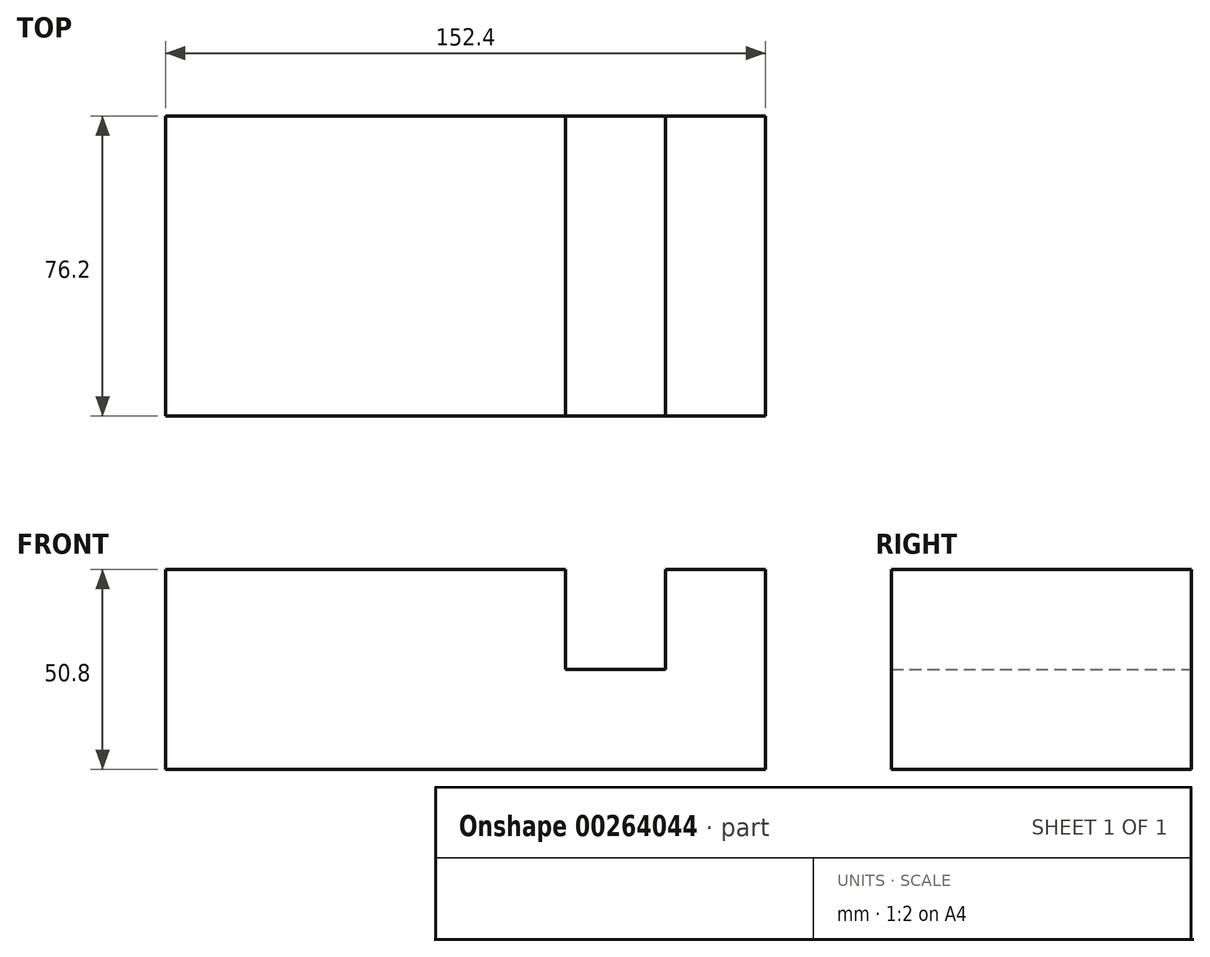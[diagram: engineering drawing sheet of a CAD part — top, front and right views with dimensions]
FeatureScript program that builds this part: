
annotation { "Feature Type Name" : "Feature", "Feature Type Description" : "" }
export const myFeature = defineFeature(function(context is Context, id is Id, definition is map)
    precondition{}
    {
        {
            var Q0;
            Q0=qCreatedBy(makeId("Front.planeOp"),FACE);
            var sketch = newSketch(context, id + "F0", { "sketchPlane" : qUnion([Q0])});
            skLineSegment(sketch, "E0.bottom", {"start": v(25.04, 0) * mm, "end": v(-76.56, 0) * mm});
            skLineSegment(sketch, "E0.right", {"start": v(-76.56, 0) * mm, "end": v(-76.56, 25.4) * mm});
            skLineSegment(sketch, "E1.bottom", {"start": v(75.84, 0) * mm, "end": v(50.44, 0) * mm});
            skLineSegment(sketch, "E1.left", {"start": v(75.84, 0) * mm, "end": v(75.84, 25.4) * mm});
            skLineSegment(sketch, "E2", {"start": v(25.04, 0) * mm, "end": v(50.44, 0) * mm});
            skLineSegment(sketch, "E3.top", {"start": v(-76.56, 50.8) * mm, "end": v(25.04, 50.8) * mm});
            skLineSegment(sketch, "E3.left", {"start": v(-76.56, 25.4) * mm, "end": v(-76.56, 50.8) * mm});
            skLineSegment(sketch, "E3.right", {"start": v(25.04, 25.4) * mm, "end": v(25.04, 50.8) * mm});
            skLineSegment(sketch, "E4.bottom", {"start": v(75.84, 25.4) * mm, "end": v(76.84, 25.4) * mm});
            skPoint(sketch, "E5.start.orphan", {"position": v(25.04, 12.7) * mm});
            skLineSegment(sketch, "E6", {"start": v(25.04, 25.4) * mm, "end": v(50.44, 25.4) * mm});
            skPoint(sketch, "E1.right.start.orphan", {"position": v(50.44, 12.7) * mm});
            skLineSegment(sketch, "E7.top", {"start": v(50.44, 50.8) * mm, "end": v(75.84, 50.8) * mm});
            skLineSegment(sketch, "E7.left", {"start": v(50.44, 25.4) * mm, "end": v(50.44, 50.8) * mm});
            skLineSegment(sketch, "E7.right", {"start": v(75.84, 25.4) * mm, "end": v(75.84, 50.8) * mm});
            skSolve(sketch);
        }
        {
            var Q0;
            Q0=makeQuery(id+"F0.imprint","IMPRINT",FACE,{"disambiguationData":[TD([[makeQuery(id+"F0.imprint","IMPRINT",EDGE,{"derivedFrom":sQuery(id+"F0.wireOp",EDGE,"E0.bottom")}),-1.0]])]});
            extrude(context, id + "F1", {"entities" : qUnion([Q0]), "depth" : 76.2 * mm});
        }
    });
